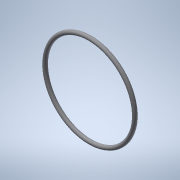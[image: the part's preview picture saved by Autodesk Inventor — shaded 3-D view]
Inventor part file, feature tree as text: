
AUTODESK INVENTOR PART (.ipt)
format: ipt  version: 2020.2 (Build 242310000, 310)  size: 121,856 bytes
history: native  units: mm
features: revolve x1, sketch x1
ambient origin geometry x8: Origin, YZ Plane, XZ Plane, XY Plane, X Axis, Y Axis, Z Axis, Center Point
bodies: Volumenkörper1 (feature_tree)
feature tree (2):
  revolve  "Umdrehung1"
  sketch  "Skizze1"  dims[d2=90.0deg d3=20.0mm]
